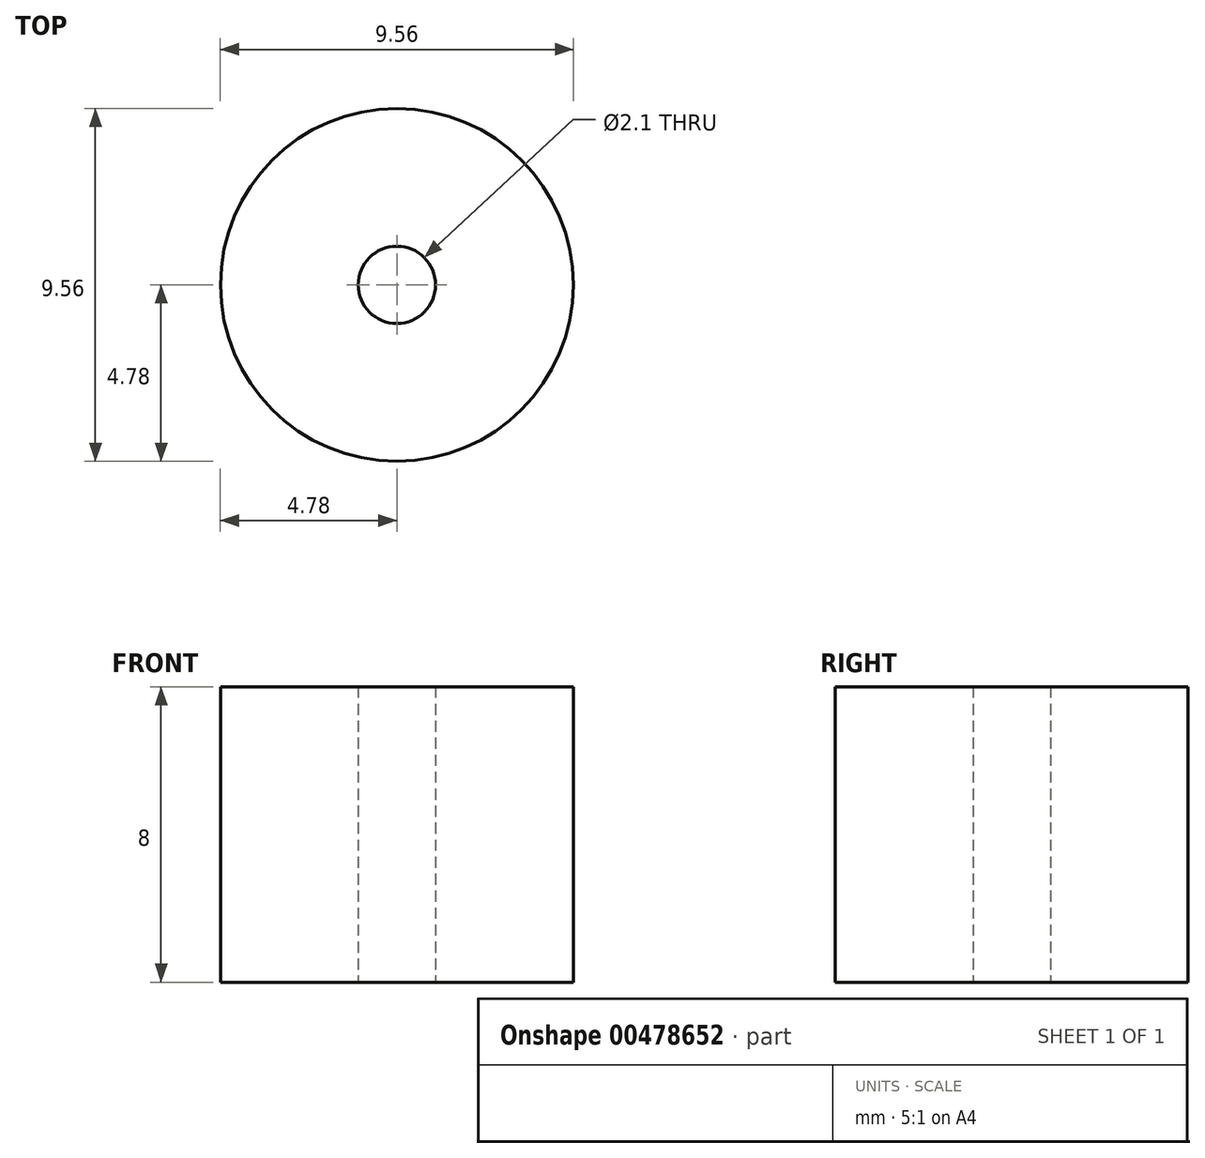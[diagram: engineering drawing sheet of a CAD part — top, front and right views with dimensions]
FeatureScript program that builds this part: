
annotation { "Feature Type Name" : "Feature", "Feature Type Description" : "" }
export const myFeature = defineFeature(function(context is Context, id is Id, definition is map)
    precondition{}
    {
        {
            var Q0;
            Q0=qCreatedBy(makeId("Top.planeOp"),FACE);
            var sketch = newSketch(context, id + "F0", { "sketchPlane" : qUnion([Q0])});
            skCircle(sketch, "E0", {"center": v(0, 0) * mm, "radius": 4.78 * mm});
            skCircle(sketch, "E1", {"center": v(0, 0) * mm, "radius": 1.05 * mm});
            skSolve(sketch);
        }
        {
            var Q0;
            Q0=makeQuery(id+"F0.imprint","IMPRINT",FACE,{"disambiguationData":[TD([[makeQuery(id+"F0.imprint","IMPRINT",EDGE,{"derivedFrom":sQuery(id+"F0.wireOp",EDGE,"E0")}),1.0]])]});
            extrude(context, id + "F1", {"entities" : qUnion([Q0]), "depth" : 8 * mm});
        }
    });
